FCSTD DOCUMENT  (FreeCAD 0.19R)
Label: fourbar
License: All rights reserved
LicenseURL: http://en.wikipedia.org/wiki/All_rights_reserved
objects: Sketcher::SketchObject×6, Spreadsheet::Sheet×3
note: 6 computed .brp shape members not serialized (recipe doc carries the construction recipe); baked Part::Feature solids carry a one-line shape summary decoded from their .brp

FEATURE [Spreadsheet::Sheet] Spreadsheet  label="Spreadsheet_C1"
  cells = G2=Input - Coupler intersection; I2=Follower - Coupler intersection; B3=Input angle; C3=Coupler angle; D3=Follower angle; E3=Transmission angle; G3=x; H3=y; I3=x; J3=y; L3=Coupler velocity; M3=Follower velocity; N3=Coupler angular velocity; O3=Follower angular velocity; Q3=Coupler acceleration; R3=Follower acceleration; S3=Coupler angular acceleration; T3=Follower angular acceleration; B4==0deg; C4==90.89528298657015deg; D4==117.2796127359781deg; E4==26.38432974940798deg; G4==30mm; H4==-7.347867213913633e-15mm; I4==29.37499999999999mm; J4==39.99511688944041mm; L4==300.0000000000001mm / s; M4==337.5000000000002mm / s; N4==-7.499999999999997rad / s; O4==-7.499999999999999rad / s; Q4==3046.426917033618mm / s ^ 2; R4==2539.212048401535mm / s ^ 2; S4==-51.34574569053257rad / s ^ 2; T4==-4.465022596683577rad / s ^ 2; B5==10deg; C5==75.01410235368648deg; D5==102.9865649519147deg; E5==27.97246259822824deg; G5==29.54423259036624mm; H5==5.20944533000791mm; I5==39.88748425127532mm; J5==43.84902536239312mm; L5==319.3629203564563mm / s; M5==289.8680177324991mm / s; N5==-7.984073008911402rad / s; O5==-6.441511505166642rad / s; Q5==2621.58330634072mm / s ^ 2; R5==3104.21808985367mm / s ^ 2; S5==15.23017048855273rad / s ^ 2; T5==55.10832556890284rad / s ^ 2; B6==20deg; C6==60.1661110945849deg; D6==92.43228189817972deg; E6==32.26617080359481deg; G6==28.19077862357725mm; H6==10.26060429977006mm; I6==48.09026397897691mm; J6==44.95945849685033mm; L6==267.8716456605167mm / s; M6==181.2312331668107mm / s; N6==-6.696791141512912rad / s; O6==-4.027360737040235rad / s; Q6==2534.924172779594mm / s ^ 2; R6==3287.316274984344mm / s ^ 2; S6==44.77606394338556rad / s ^ 2; T6==71.22809229113979rad / s ^ 2; B7==30deg; C7==48.43792685783198deg; D7==86.79230151730125deg; E7==38.35437465946926deg; G7==25.98076211353316mm; H7==15mm; I7==52.51800464844848mm; J7==44.92949646491035mm; L7==202.2543968467237mm / s; M7==76.45409046702568mm / s; N7==-5.056359921168088rad / s; O7==-1.698979788156125rad / s; Q7==1953.243892061024mm / s ^ 2; R7==2603.197835290744mm / s ^ 2; S7==41.60307736707902rad / s ^ 2; T7==57.77678003525764rad / s ^ 2; B8==40deg; C8==39.71705767707306deg; D8==85.22018205167336deg; E8==45.5031243746003deg; G8==22.98133329356934mm; H8==19.28362829059618mm; I8==53.74970736185978mm; J8==44.84350225729938mm; L8==149.2703289481105mm / s; M8==1.038483142432828mm / s; N8==-3.731758223702759rad / s; O8==0.02307740316517394rad / s; Q8==1348.652545807255mm / s ^ 2; R8==1832.793913604046mm / s ^ 2; S8==30.70595688742105rad / s ^ 2; T8==40.72875363216355rad / s ^ 2; B9==50deg; C9==33.25667684687866deg; D9==86.51870772172988deg; E9==53.26203087485123deg; G9==19.28362829060056mm; H9==22.98133329357076mm; I9==52.73251852802909mm; J9==44.9169605215469mm; L9==111.3864171490056mm / s; M9==53.92289844380171mm / s; N9==-2.784660428725138rad / s; O9==1.198286632084482rad / s; Q9==912.7844608979208mm / s ^ 2; R9==1258.258699991039mm / s ^ 2; S9==21.4617095976343rad / s ^ 2; T9==27.92441160853883rad / s ^ 2; B10==60deg; C10==28.3900210720747deg; D10==89.75903123514748deg; E10==61.36901016307278deg; G10==15.0000000000002mm; H10==25.98076211353359mm; I10==50.18925586742708mm; J10==44.99960202287071mm; L10==84.82507896940315mm / s; M10==89.57273781285126mm / s; N10==-2.120626974235077rad / s; O10==1.990505284730027rad / s; Q10==629.1936677826678mm / s ^ 2; R10==889.2026480291986mm / s ^ 2; S10==15.07330030917509rad / s ^ 2; T10==19.35876028310667rad / s ^ 2; B11==70deg; C11==24.64817432965277deg; D11==94.31266865982101deg; E11==69.66449433016822deg; G11==10.26060429977023mm; H11==28.1907786235778mm; I11==46.61603544097609mm; J11==44.87258387772556mm; L11==65.86233169509796mm / s; M11==113.8085738373253mm / s; N11==-1.646558292377448rad / s; O11==2.529079418607227rad / s; Q11==449.0893536527395mm / s ^ 2; R11==680.4722185552483mm / s ^ 2; S11==10.89497235316264rad / s ^ 2; T11==13.70222655977709rad / s ^ 2; B12==80deg; C12==21.72184925731659deg; D12==99.76313478132045deg; E12==78.04128552400385deg; G12==5.209445330007912mm; H12==29.54423259036624mm; I12==42.36910549817785mm; J12==44.34827447716609mm; L12==51.84505524769817mm / s; M12==130.4221299546489mm / s; N12==-1.296126381192453rad / s; O12==2.89826955454775rad / s; Q12==335.3933317684076mm / s ^ 2; R12==583.0285716313424mm / s ^ 2; S12==8.214817033012773rad / s ^ 2; T12==9.86425040584497rad / s ^ 2; B13==90deg; C13==19.41122601563446deg; D13==105.8279043171625deg; E13==86.41667830152804deg; G13==1.832281627259899e-15mm; H13==30mm; I13==37.72630236809285mm; J13==43.29383728015474mm; L13==40.99246719218419mm / s; M13==141.7507617343376mm / s; N13==-1.024811679804604rad / s; O13==3.150016927429723rad / s; Q13==265.1680425136465mm / s ^ 2; R13==549.6797887551762mm / s ^ 2; S13==6.545479724086622rad / s ^ 2; T13==7.123952707572676rad / s ^ 2; B14==100deg; C14==17.59046378483668deg; D14==112.3058886296495deg; E14==94.7154248448129deg; G14==-5.20944533000791mm; H14==29.54423259036625mm; I14==32.92019389146202mm; J14==41.6326821535047mm; L14==32.07819562989725mm / s; M14==149.1905975151657mm / s; N14==-0.8019548907474308rad / s; O14==3.315346611448124rad / s; Q14==225.4771028839006mm / s ^ 2; R14==543.6771385419606mm / s ^ 2; S14==5.60011911819432rad / s ^ 2; T14==5.01539993606897rad / s ^ 2; B15==110deg; C15==16.18647957776968deg; D15==119.0433786689153deg; E15==102.8568990911456deg; G15==-10.26060429977006mm; H15==28.19077862357725mm; +394 more cells
FEATURE [Spreadsheet::Sheet] Spreadsheet001  label="Spreadsheet_C2"
  cells = G2=Input - Coupler intersection; I2=Follower - Coupler intersection; B3=Input angle; C3=Coupler angle; D3=Follower angle; E3=Transmission angle; G3=x; H3=y; I3=x; J3=y; L3=Coupler velocity; M3=Follower velocity; N3=Coupler angular velocity; O3=Follower angular velocity; Q3=Coupler acceleration; R3=Follower acceleration; S3=Coupler angular acceleration; T3=Follower angular acceleration; B4==0deg; C4==269.1047170134299deg; D4==242.7203872640219deg; E4==333.615670250592deg; G4==30mm; H4==-7.347865035119899e-15mm; I4==29.375mm; J4==-39.99511688944042mm; L4==300.0000000000003mm / s; M4==337.5000000000002mm / s; N4==-7.500000000000004rad / s; O4==-7.5rad / s; Q4==2890.065508525489mm / s ^ 2; R4==2532.19228686293mm / s ^ 2; S4==45.34574569053223rad / s ^ 2; T4==-1.534977403317279rad / s ^ 2; B5==10deg; C5==256.4104344555273deg; D5==228.437971857299deg; E5==332.0275374017718deg; G5==29.54423259036624mm; H5==5.20944533000791mm; I5==20.14562859280927mm; J5==-33.6707069703253mm; L5==198.8074206450332mm / s; M5==293.0736158941766mm / s; N5==-4.970185516125825rad / s; O5==-6.512747019870586rad / s; Q5==3523.157972089841mm / s ^ 2; R5==2771.845712802928mm / s ^ 2; S5==84.54392790651025rad / s ^ 2; T5==44.66577282616023rad / s ^ 2; B6==20deg; C6==249.442648761194deg; D6==217.1764779575994deg; E6==327.7338291964054deg; G6==28.19077862357725mm; H6==10.26060429977006mm; I6==14.14498724363285mm; J6==-27.19224264824029mm; L6==82.97670262028444mm / s; M6==213.4731586490914mm / s; N6==-2.07441756550711rad / s; O6==-4.743847969979806rad / s; Q6==2938.375286824446mm / s ^ 2; R6==2340.121878689478mm / s ^ 2; S6==73.33323412863224rad / s ^ 2; T6==46.88120578087823rad / s ^ 2; B7==30deg; C7==247.5925657022089deg; D7==209.2381910427464deg; E7==321.6456253405375deg; G7==25.98076211353318mm; H7==15.00000000000001mm; I7==10.73314868394847mm; J7==-21.97986323260324mm; L7==3.213983617450931mm / s; M7==147.4663744159239mm / s; N7==0.08034959043627322rad / s; O7==-3.277030542576084rad / s; Q7==1988.290086253973mm / s ^ 2; R7==1584.500745937608mm / s ^ 2; S7==49.70725173708786rad / s ^ 2; T7==33.53354906891722rad / s ^ 2; B8==40deg; C8==249.2509015630467deg; D8==203.7477771884464deg; E8==314.4968756253997deg; G8==22.98133329356934mm; H8==19.28362829059618mm; I8==8.810280358627262mm; J8==-18.12200308644476mm; L8==58.85406668526655mm / s; M8==102.7567781881251mm / s; N8==1.471351667131663rad / s; O8==-2.283483959736112rad / s; Q8==1279.79723597622mm / s ^ 2; R8==1012.996629876752mm / s ^ 2; S8==31.92160579197796rad / s ^ 2; T8==21.8988090468907rad / s ^ 2; B9==50deg; C9==253.1372204737326deg; D9==199.8751895988861deg; E9==306.7379691251534deg; G9==19.28362829059653mm; H9==22.9813332935698mm; I9==7.680405601046743mm; J9==-15.29875582880347mm; L9==93.94151543084419mm / s; M9==73.54841287673226mm / s; N9==2.348537885771103rad / s; O9==-1.634409175038493rad / s; Q9==861.1241483436276mm / s ^ 2; R9==656.7035027555165mm / s ^ 2; S9==20.80954282954652rad / s ^ 2; T9==14.34684081864775rad / s ^ 2; B10==60deg; C10==258.4364278206647deg; D10==197.0674176575901deg; E10==298.6309898369254deg; G10==15.00000000000023mm; H10==25.98076211353364mm; I10==6.981796764154542mm; J10==-13.20735364709915mm; L10==116.4040263376699mm / s; M10==54.04642202361052mm / s; N10==2.910100658441746rad / s; O10==-1.201031600524678rad / s; Q10==655.5127264508859mm / s ^ 2; R10==443.2843201637248mm / s ^ 2; S10==14.03003721277936rad / s ^ 2; T10==9.744577238848901rad / s ^ 2; B11==70deg; C11==264.6487154718823deg; D11==194.9842211417089deg; E11==290.3355056698266deg; G11==10.26060429977016mm; H11==28.19077862357765mm; I11==6.530132002076741mm; J11==-11.63488617233238mm; L11==131.0653031434319mm / s; M11==40.45523095782687mm / s; N11==3.276632578585795rad / s; O11==-0.8990051323961521rad / s; Q11==580.5467618746452mm / s ^ 2; R11==315.2559392094245mm / s ^ 2; S11==9.766166054540237rad / s ^ 2; T11==6.958911847921672rad / s ^ 2; B12==80deg; C12==271.4597804848207deg; D12==193.4184949608529deg; E12==281.9587144760322deg; G12==5.209445330035601mm; H12==29.54423259038184mm; I12==6.228454109950706mm; J12==-10.44278556685611mm; L12==140.6974918637275mm / s; M12==30.46313876069064mm / s; N12==3.517437296593184rad / s; O12==-0.6769586391264583rad / s; Q12==567.2560861570064mm / s ^ 2; R12==238.5569913802688mm / s ^ 2; S12==6.930854781777549rad / s ^ 2; T12==5.281421408911355rad / s ^ 2; B13==90deg; C13==278.6612609202185deg; D13==192.2445826186905deg; E13==273.583321698472deg; G13==1.73068408173047e-15mm; H13==30mm; I13==6.023697631907162mm; J13==-9.543837280154765mm; L13==146.8748201333606mm / s; M13==22.63311467551413mm / s; N13==3.671870503334013rad / s; O13==-0.5029581039003137rad / s; Q13==573.7348543438629mm / s ^ 2; R13==194.5305694431621mm / s ^ 2; S13==4.893966642695538rad / s ^ 2; T13==4.31549365920935rad / s ^ 2; B14==100deg; C14==286.1043891278963deg; D14==191.3889642830835deg; E14==265.2845751551871deg; G14==-5.20944533000791mm; H14==29.54423259036625mm; I14==5.886084778763305mm; J14==-8.886083718575996mm; L14==150.4652074055786mm / s; M14==16.00520926752417mm / s; N14==3.761630185139463rad / s; O14==-0.3556713170560924rad / s; Q14==580.9175521683676mm / s ^ 2; R14==173.5850863101949mm / s ^ 2; S14==3.270652351392986rad / s ^ 2; T14==3.855371533518331rad / s ^ 2; B15==110deg; C15==293.6717802451079deg; D15==190.8148811539623deg; E15==257.1431009088545deg; G15==-10.26060429977006mm; H15==28.19077862357726mm; +394 more cells
FEATURE [Spreadsheet::Sheet] Spreadsheet002  label="Spreadsheet_InputParameters"
  cells = A1=FrameL; B1==5cm; D1=InputVelocity; E1==5 * B2; A2=CrankL; B2==3cm; D2=InputAcceleration; E2==2 * B2; A3=CouplerL; B3==4cm; A4=FollowerL; B4==4.5cm; A5=End; A6=Datums for configuration; D6=Datums for analysis
FEATURE [Sketcher::SketchObject] Sketch  label="Sketch_C1"
  FullyConstrained = true
  sketch-geometry (4):
    g0: LineSegment StartX=0 StartY=0 StartZ=0 EndX=30 EndY=-7.3e-15 EndZ=0
    g1: LineSegment StartX=30 StartY=-7.3e-15 StartZ=0 EndX=29.375 EndY=39.9951 EndZ=0
    g2: LineSegment StartX=29.375 StartY=39.9951 StartZ=0 EndX=50 EndY=0 EndZ=0
    g3: LineSegment StartX=50 StartY=0 StartZ=0 EndX=0 EndY=0 EndZ=0
  constraints (11):
    c: Coincident(g1,g0)
    c: Coincident(g2,g1)  'TmpConstraint'
    c: Coincident(g0,g-1)
    c: Distance(g0) = 30  'CrankL'
    c: Distance(g1) = 40  'CouplerL'
    c: Distance(g2) = 45  'FollowerL'
    c: Coincident(g3,g2)
    c: Coincident(g3,g0)
    c: Horizontal(g3)
    c: Angle(g3,g0) = 0  'InputAngle'
    c: Distance(g3) = 50  'FrameL'
FEATURE [Sketcher::SketchObject] Sketch001  label="Sketch_V1"
  ExternalGeometry = -> [Sketch]
  FullyConstrained = true
  MapMode = 2
  Support = -> [Sketch]
  sketch-geometry (3):
    g0: LineSegment StartX=0 StartY=0 StartZ=0 EndX=4.24e-14 EndY=150 EndZ=0
    g1: LineSegment StartX=4.24e-14 StartY=150 StartZ=0 EndX=299.963 EndY=154.688 EndZ=0
    g2: LineSegment StartX=299.963 StartY=154.688 StartZ=0 EndX=0 EndY=0 EndZ=0
  constraints (8):
    c: Coincident(g1,g0)
    c: Coincident(g2,g1)
    c: Coincident(g2,g0)
    c: Coincident(g0,g-1)
    c: Angle(g-3,g0) = 1.5708
    c: Distance(g0) = 150  'InputVelocity'
    c: Perpendicular(g1,g-4)
    c: Perpendicular(g-5,g2)
FEATURE [Sketcher::SketchObject] Sketch002  label="Sketch_A1"
  ExternalGeometry = -> [Sketch]
  FullyConstrained = true
  MapMode = 2
  Support = -> [Sketch001]
  sketch-geometry (6):
    g0: LineSegment StartX=0 StartY=0 StartZ=0 EndX=1.58878e-11 EndY=60 EndZ=0
    g1: LineSegment StartX=1.58878e-11 StartY=60 StartZ=0 EndX=-750 EndY=60 EndZ=0
    g2: LineSegment StartX=-750 StartY=60 StartZ=0 EndX=2446.37 EndY=109.949 EndZ=0
    g3: LineSegment StartX=2446.37 StartY=109.949 StartZ=0 EndX=2461.81 EndY=-878.04 EndZ=0
    g4: LineSegment StartX=2461.81 StartY=-878.04 StartZ=0 EndX=874.827 EndY=-1696.43 EndZ=0
    g5: LineSegment StartX=874.827 StartY=-1696.43 StartZ=0 EndX=0 EndY=0 EndZ=0
  constraints (17):
    c: Coincident(g0,g-1)
    c: Coincident(g1,g0)
    c: Coincident(g2,g1)
    c: Coincident(g3,g2)
    c: Coincident(g4,g3)
    c: Coincident(g5,g4)
    c: Coincident(g5,g0)
    c: Angle(g-3,g0) = 1.5708
    c: Distance(g0) = 60  'InputAcceleration'
    c: Distance(g1) = 750  'RadialCrank'
    c: Distance(g3) = 988.11  'RadialCoupler'
    c: Distance(g5) = 1908.71  'RadialFollower'
    c: Angle(g3,g-4) = 0
    c: Perpendicular(g2,g3)
    c: Angle(g5,g-5) = 0
    c: Perpendicular(g5,g4)
    c: Angle(g1,g-3) = 0
FEATURE [Sketcher::SketchObject] Sketch003  label="Sketch_C2"
  FullyConstrained = true
  MapMode = 2
  Support = -> [Sketch002]
  sketch-geometry (4):
    g0: LineSegment StartX=0 StartY=0 StartZ=0 EndX=30 EndY=-7.3e-15 EndZ=0
    g1: LineSegment StartX=30 StartY=-7.3e-15 StartZ=0 EndX=29.375 EndY=-39.9951 EndZ=0
    g2: LineSegment StartX=29.375 StartY=-39.9951 StartZ=0 EndX=50 EndY=0 EndZ=0
    g3: LineSegment StartX=50 StartY=0 StartZ=0 EndX=0 EndY=0 EndZ=0
  constraints (11):
    c: Coincident(g0,g-1)
    c: Coincident(g1,g0)
    c: Coincident(g2,g1)  'TmpConstraint'
    c: Coincident(g3,g2)
    c: Coincident(g3,g0)
    c: Horizontal(g3)
    c: Angle(g3,g0) = 0  'InputAngle'
    c: Distance(g3) = 50  'FrameL'
    c: Distance(g1) = 40  'CouplerL'
    c: Distance(g2) = 45  'FollowerL'
    c: Distance(g0) = 30  'CrankL'
FEATURE [Sketcher::SketchObject] Sketch004  label="Sketch_V2"
  ExternalGeometry = -> [Sketch003]
  FullyConstrained = true
  MapMode = 2
  Support = -> [Sketch003]
  sketch-geometry (3):
    g0: LineSegment StartX=0 StartY=0 StartZ=0 EndX=4.24e-14 EndY=150 EndZ=0
    g1: LineSegment StartX=4.24e-14 StartY=150 StartZ=0 EndX=-299.963 EndY=154.687 EndZ=0
    g2: LineSegment StartX=-299.963 StartY=154.687 StartZ=0 EndX=0 EndY=0 EndZ=0
  constraints (8):
    c: Coincident(g0,g-1)
    c: Coincident(g1,g0)
    c: Coincident(g2,g1)
    c: Coincident(g2,g0)
    c: Distance(g0) = 150  'InputVelocity'
    c: Angle(g-3,g0) = 1.5708
    c: Perpendicular(g-4,g1)
    c: Perpendicular(g-5,g2)
FEATURE [Sketcher::SketchObject] Sketch005  label="Sketch_A2"
  ExternalGeometry = -> [Sketch003]
  FullyConstrained = true
  MapMode = 2
  Support = -> [Sketch004]
  sketch-geometry (6):
    g0: LineSegment StartX=0 StartY=0 StartZ=0 EndX=1.7e-14 EndY=60 EndZ=0
    g1: LineSegment StartX=1.7e-14 StartY=60 StartZ=0 EndX=-750 EndY=60 EndZ=0
    g2: LineSegment StartX=-750 StartY=60 StartZ=0 EndX=-1034.85 EndY=64.4513 EndZ=0
    g3: LineSegment StartX=-1034.85 StartY=64.4513 StartZ=0 EndX=-995.008 EndY=2613.96 EndZ=0
    g4: LineSegment StartX=-995.008 StartY=2613.96 StartZ=0 EndX=855.795 EndY=1659.52 EndZ=0
    g5: LineSegment StartX=855.795 StartY=1659.52 StartZ=0 EndX=0 EndY=0 EndZ=0
  constraints (17):
    c: Coincident(g0,g-1)
    c: Coincident(g1,g0)
    c: Coincident(g2,g1)
    c: Coincident(g3,g2)
    c: Coincident(g4,g3)
    c: Coincident(g5,g4)
    c: Coincident(g5,g0)
    c: Distance(g0) = 60  'InputAcceleration'
    c: Distance(g1) = 750  'RadialCrank'
    c: Distance(g3) = 2549.82  'RadialCoupler'
    c: Distance(g5) = 1867.19  'RadialFollower'
    c: Angle(g-3,g0) = 1.5708
    c: Angle(g-3,g1) = 0
    c: Angle(g3,g-4) = 0
    c: Angle(g5,g-5) = 0
    c: Perpendicular(g3,g2)
    c: Perpendicular(g5,g4)
